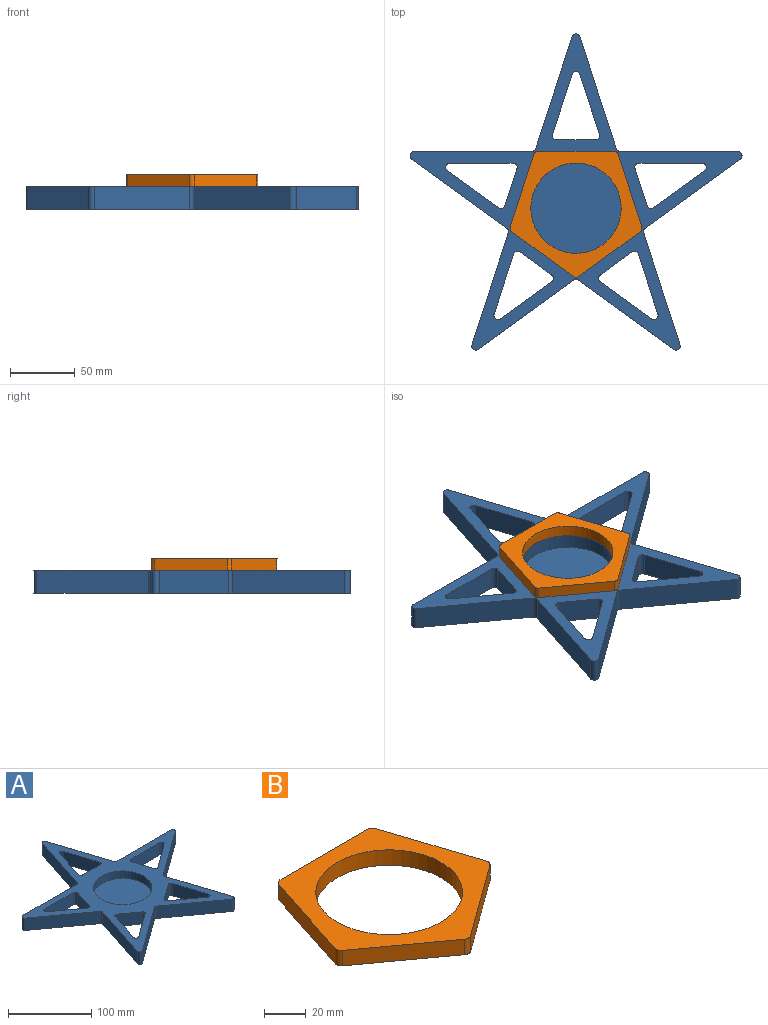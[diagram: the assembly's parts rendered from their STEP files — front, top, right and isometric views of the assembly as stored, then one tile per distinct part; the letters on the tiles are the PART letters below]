
ASSEMBLY  parts=2 mates=1
PART A: 54 faces, bbox 257.3x245.1x18 mm
  f0: cylinder r=3.25mm len=18mm, axis (0,0,-1), area 110.3mm2, adj f1,f44,f45,f46
  f1: plane 28.74x18mm, normal (-0.95,0.31,0), area 543.9mm2, adj f0,f2,f45,f46
  f2: cylinder r=3.25mm len=18mm, axis (0,0,-1), area 110.3mm2, adj f1,f3,f45,f46
  f3: plane 39.55x28.74mm, normal (0.59,0.81,0), area 880mm2, adj f2,f4,f45,f46
  f4: cylinder r=3.25mm len=18mm, axis (0,0,-1), area 147mm2, adj f3,f44,f45,f46
  f5: cylinder r=3.25mm len=18mm, axis (0,0,-1), area 110.3mm2, adj f6,f39,f45,f46
  f6: plane 24.44x18mm, normal (-0.59,-0.81,0), area 543.9mm2, adj f5,f7,f45,f46
  f7: cylinder r=3.25mm len=18mm, axis (0,0,-1), area 110.3mm2, adj f6,f8,f45,f46
  f8: plane 39.55x28.74mm, normal (-0.59,0.81,0), area 880mm2, adj f7,f9,f45,f46
  f9: cylinder r=3.25mm len=18mm, axis (0,0,-1), area 147mm2, adj f8,f39,f45,f46
  f10: cylinder r=3.25mm len=18mm, axis (0,0,-1), area 110.3mm2, adj f11,f40,f45,f46
  f11: plane 24.44x18mm, normal (0.59,-0.81,0), area 543.9mm2, adj f10,f12,f45,f46
  f12: cylinder r=3.25mm len=18mm, axis (0,0,-1), area 110.3mm2, adj f11,f13,f45,f46
  f13: plane 46.5x18mm, normal (-0.95,-0.31,0), area 880mm2, adj f12,f14,f45,f46
  f14: cylinder r=3.25mm len=18mm, axis (0,0,-1), area 147mm2, adj f13,f40,f45,f46
  f15: cylinder r=3.25mm len=18mm, axis (0,0,-1), area 110.3mm2, adj f16,f41,f45,f46
  f16: plane 28.74x18mm, normal (0.95,0.31,0), area 543.9mm2, adj f15,f17,f45,f46
  f17: cylinder r=3.25mm len=18mm, axis (0,0,-1), area 110.3mm2, adj f16,f18,f45,f46
  f18: plane 48.89x18mm, normal (0,-1,0), area 880mm2, adj f17,f19,f45,f46
  f19: cylinder r=3.25mm len=18mm, axis (0,0,-1), area 147mm2, adj f18,f41,f45,f46
  f20: cylinder r=3.25mm len=18mm, axis (0,0,-1), area 73.5mm2, adj f21,f42,f45,f46
  f21: plane 86.63x28.15mm, normal (0.95,0.31,0), area 1639.6mm2, adj f20,f45,f46,f49
  f22: plane 86.63x28.15mm, normal (-0.95,0.31,0), area 1639.6mm2, adj f23,f45,f46,f49
  f23: cylinder r=3.25mm len=18mm, axis (0,0,-1), area 73.5mm2, adj f22,f24,f45,f46
  f24: plane 91.09x18mm, normal (0,1,0), area 1639.6mm2, adj f23,f45,f46,f50
  f25: plane 73.69x53.54mm, normal (-0.59,-0.81,0), area 1639.6mm2, adj f26,f45,f46,f50
  f26: cylinder r=3.25mm len=18mm, axis (0,0,-1), area 73.5mm2, adj f25,f27,f45,f46
  f27: plane 86.63x28.15mm, normal (-0.95,0.31,0), area 1639.6mm2, adj f26,f45,f46,f51
  f28: plane 73.69x53.54mm, normal (0.59,-0.81,0), area 1639.6mm2, adj f29,f45,f46,f51
  f29: cylinder r=3.25mm len=18mm, axis (0,0,-1), area 73.5mm2, adj f28,f30,f45,f46
  f30: plane 73.69x53.54mm, normal (-0.59,-0.81,0), area 1639.6mm2, adj f29,f45,f46,f52
  f31: plane 86.63x28.15mm, normal (0.95,0.31,0), area 1639.6mm2, adj f32,f45,f46,f52
  f32: cylinder r=3.25mm len=18mm, axis (0,0,-1), area 73.5mm2, adj f31,f33,f45,f46
  f33: plane 73.69x53.54mm, normal (0.59,-0.81,0), area 1639.6mm2, adj f32,f45,f46,f53
  f34: plane 46.5x18mm, normal (-0.95,-0.31,0), area 880mm2, adj f35,f43,f45,f46
  f35: cylinder r=3.25mm len=18mm, axis (0,0,-1), area 110.3mm2, adj f34,f36,f45,f46
  f36: plane 30.21x18mm, normal (0,1,0), area 543.9mm2, adj f35,f37,f45,f46
  f37: cylinder r=3.25mm len=18mm, axis (0,0,-1), area 110.3mm2, adj f36,f38,f45,f46
  f38: plane 46.5x18mm, normal (0.95,-0.31,0), area 880mm2, adj f37,f43,f45,f46
  f39: plane 46.5x18mm, normal (0.95,-0.31,0), area 880mm2, adj f5,f9,f45,f46
  f40: plane 39.55x28.74mm, normal (0.59,0.81,0), area 880mm2, adj f10,f14,f45,f46
  f41: plane 39.55x28.74mm, normal (-0.59,0.81,0), area 880mm2, adj f15,f19,f45,f46
  f42: plane 91.09x18mm, normal (0,1,0), area 1639.6mm2, adj f20,f45,f46,f53
  f43: cylinder r=3.25mm len=18mm, axis (0,0,-1), area 147mm2, adj f34,f38,f45,f46
  f44: plane 48.89x18mm, normal (0,-1,0), area 880mm2, adj f0,f4,f45,f46
  f45: plane 257.33x245.05mm, normal (0,0,1), area 13061.8mm2, adj f0,f1,f2,f3,f4,f5,f6,f7
  f46: plane 257.33x245.05mm, normal (0,0,-1), area 16910.2mm2, adj f0,f1,f2,f3,f4,f5,f6,f7
  f47: cylinder r=35mm len=70mm, axis (0,0,1), area 2419mm2, adj f45,f48
  f48: plane 70x70mm, normal (0,0,1), area 3848.5mm2, adj f47
  f49: cylinder r=3.25mm len=18mm, axis (0,0,-1), area 147mm2, adj f21,f22,f45,f46
  f50: cylinder r=3.25mm len=18mm, axis (0,0,-1), area 147mm2, adj f24,f25,f45,f46
  f51: cylinder r=3.25mm len=18mm, axis (0,0,-1), area 147mm2, adj f27,f28,f45,f46
  f52: cylinder r=3.25mm len=18mm, axis (0,0,-1), area 147mm2, adj f30,f31,f45,f46
  f53: cylinder r=3.25mm len=18mm, axis (0,0,-1), area 147mm2, adj f33,f42,f45,f46
PART B: 13 faces, bbox 102.3x97.6x9 mm
  f0: cylinder r=3.25mm len=9mm, axis (0,0,-1), area 36.8mm2, adj f1,f10,f11,f12
  f1: plane 56.32x18.3mm, normal (0.95,0.31,0), area 532.9mm2, adj f0,f2,f11,f12
  f2: cylinder r=3.25mm len=9mm, axis (0,0,-1), area 36.8mm2, adj f1,f3,f11,f12
  f3: plane 59.21x9mm, normal (0,1,0), area 532.9mm2, adj f2,f4,f11,f12
  f4: cylinder r=3.25mm len=9mm, axis (0,0,-1), area 36.8mm2, adj f3,f5,f11,f12
  f5: plane 56.32x18.3mm, normal (-0.95,0.31,0), area 532.9mm2, adj f4,f6,f11,f12
  f6: cylinder r=3.25mm len=9mm, axis (0,0,-1), area 36.8mm2, adj f5,f7,f11,f12
  f7: plane 47.9x34.8mm, normal (-0.59,-0.81,0), area 532.9mm2, adj f6,f8,f11,f12
  f8: cylinder r=3.25mm len=9mm, axis (0,0,-1), area 36.8mm2, adj f7,f10,f11,f12
  f9: cylinder r=35mm len=70mm, axis (0,0,-1), area 1979.2mm2, adj f11,f12
  f10: plane 47.9x34.8mm, normal (0.59,-0.81,0), area 532.9mm2, adj f0,f8,f11,f12
  f11: plane 102.31x97.62mm, normal (0,0,1), area 3179.3mm2, adj f0,f1,f2,f3,f4,f5,f6,f7
  f12: plane 102.31x97.62mm, normal (0,0,-1), area 3179.3mm2, adj f0,f1,f2,f3,f4,f5,f6,f7
PLACE A at identity fixed
PLACE B t=(0,0,18)mm
MATE fastened B.f9 <-> A.f47  axis (0,0,-1) through (0,0,18)mm
